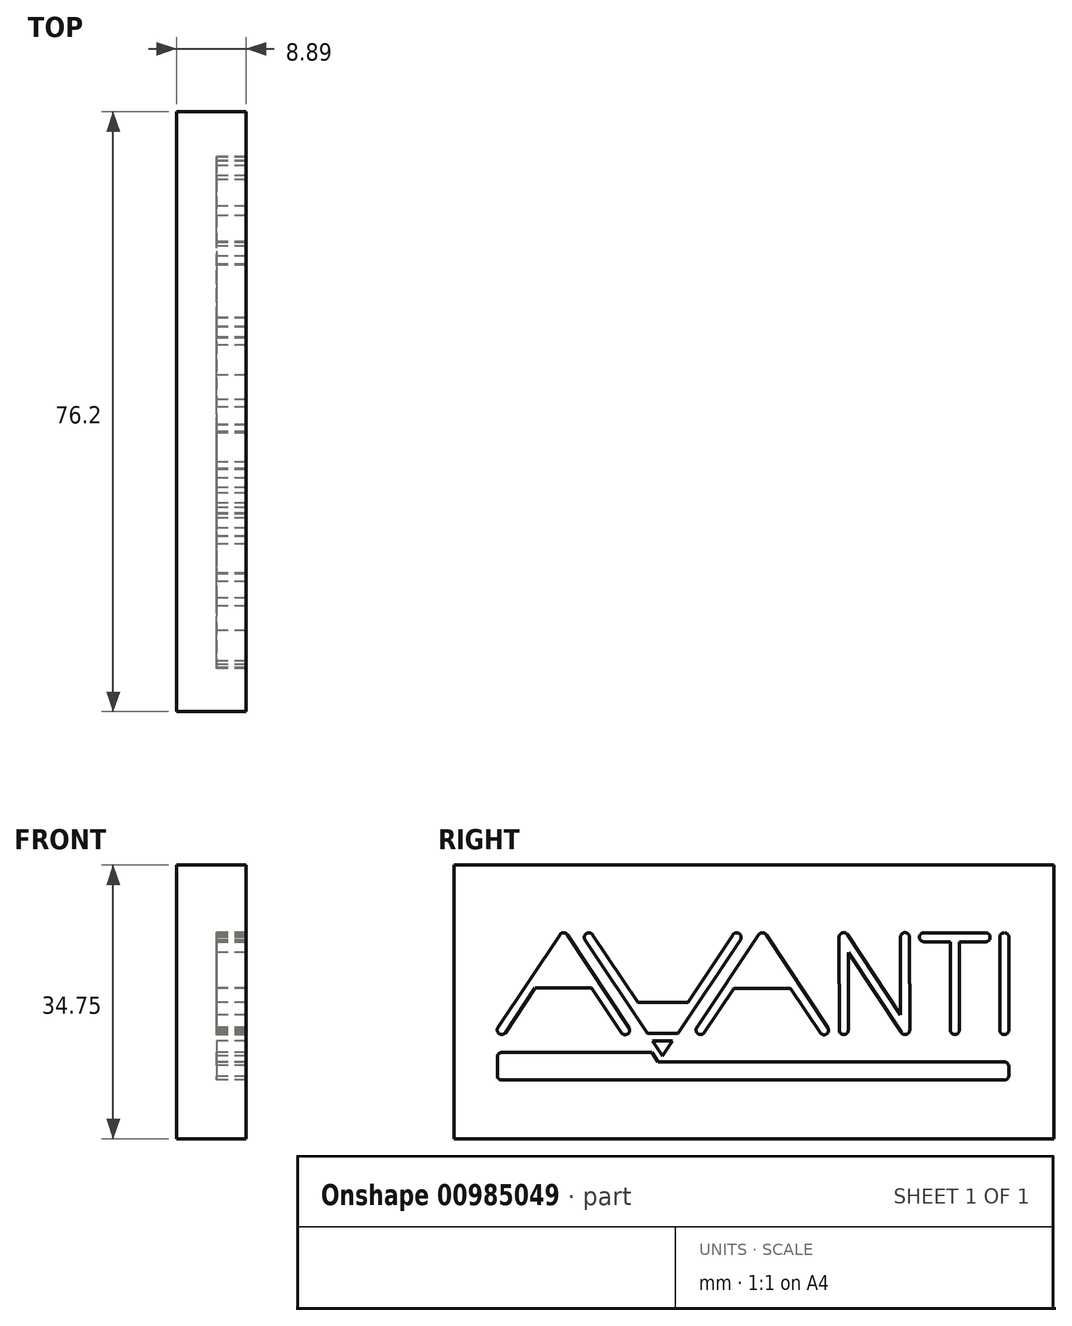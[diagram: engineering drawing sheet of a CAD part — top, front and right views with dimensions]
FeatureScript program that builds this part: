
annotation { "Feature Type Name" : "Feature", "Feature Type Description" : "" }
export const myFeature = defineFeature(function(context is Context, id is Id, definition is map)
    precondition{}
    {
        {
            var Q0;
            Q0=qCreatedBy(makeId("Right.planeOp"),FACE);
            var sketch = newSketch(context, id + "F0", { "sketchPlane" : qUnion([Q0])});
            skArc(sketch, "E0", {"start": v(-1.7, 15.63) * mm, "mid": v(-1.88, 16.42) * mm, "end": v(-2.67, 16.26) * mm});
            skLineSegment(sketch, "E1", {"start": v(-1.7, 15.63) * mm, "end": v(-9.65, 3.71) * mm});
            skLineSegment(sketch, "E2", {"start": v(-9.65, 3.71) * mm, "end": v(-13.5, 3.71) * mm});
            skLineSegment(sketch, "E3", {"start": v(-13.5, 3.71) * mm, "end": v(-21.48, 15.64) * mm});
            skArc(sketch, "E4", {"start": v(-20.5, 16.26) * mm, "mid": v(-21.28, 16.42) * mm, "end": v(-21.48, 15.64) * mm});
            skLineSegment(sketch, "E5", {"start": v(-20.5, 16.26) * mm, "end": v(-14.76, 7.69) * mm});
            skLineSegment(sketch, "E6", {"start": v(-14.76, 7.69) * mm, "end": v(-8.41, 7.69) * mm});
            skLineSegment(sketch, "E7", {"start": v(-8.41, 7.69) * mm, "end": v(-2.67, 16.26) * mm});
            skArc(sketch, "E8", {"start": v(1.57, 16.27) * mm, "mid": v(1.08, 16.52) * mm, "end": v(0.6, 16.27) * mm});
            skLineSegment(sketch, "E9", {"start": v(1.57, 16.27) * mm, "end": v(9.4, 4.42) * mm});
            skArc(sketch, "E10", {"start": v(8.43, 3.81) * mm, "mid": v(9.21, 3.65) * mm, "end": v(9.4, 4.42) * mm});
            skLineSegment(sketch, "E11", {"start": v(4.63, 9.48) * mm, "end": v(8.43, 3.81) * mm});
            skLineSegment(sketch, "E12", {"start": v(-2.54, 9.48) * mm, "end": v(4.63, 9.48) * mm});
            skLineSegment(sketch, "E13", {"start": v(-6.33, 3.8) * mm, "end": v(-2.54, 9.48) * mm});
            skArc(sketch, "E14", {"start": v(-7.25, 4.5) * mm, "mid": v(-7.13, 3.71) * mm, "end": v(-6.33, 3.8) * mm});
            skLineSegment(sketch, "E15", {"start": v(-7.25, 4.5) * mm, "end": v(0.6, 16.27) * mm});
            skLineSegment(sketch, "E16", {"start": v(-12.86, 2.8) * mm, "end": v(-11.6, 0.86) * mm});
            skLineSegment(sketch, "E17", {"start": v(-10.32, 2.8) * mm, "end": v(-12.86, 2.8) * mm});
            skLineSegment(sketch, "E18", {"start": v(-11.6, 0.86) * mm, "end": v(-10.32, 2.8) * mm});
            skLineSegment(sketch, "E19", {"start": v(-32.6, 0.86) * mm, "end": v(-32.6, -1.7) * mm});
            skArc(sketch, "E20", {"start": v(-32.13, 1.3) * mm, "mid": v(-32.42, 1.15) * mm, "end": v(-32.6, 0.86) * mm});
            skLineSegment(sketch, "E21", {"start": v(-12.97, 1.3) * mm, "end": v(-32.13, 1.3) * mm});
            skLineSegment(sketch, "E22", {"start": v(-12.19, 0.1) * mm, "end": v(-12.97, 1.3) * mm});
            skLineSegment(sketch, "E23", {"start": v(31.9, 0.1) * mm, "end": v(-12.19, 0.1) * mm});
            skArc(sketch, "E24", {"start": v(32.36, -0.34) * mm, "mid": v(32.2, -0.05) * mm, "end": v(31.9, 0.1) * mm});
            skLineSegment(sketch, "E25", {"start": v(32.36, -0.34) * mm, "end": v(32.36, -1.73) * mm});
            skArc(sketch, "E26", {"start": v(31.9, -2.18) * mm, "mid": v(32.2, -2.03) * mm, "end": v(32.36, -1.73) * mm});
            skLineSegment(sketch, "E27", {"start": v(-32.1, -2.18) * mm, "end": v(31.9, -2.18) * mm});
            skArc(sketch, "E28", {"start": v(-32.6, -1.7) * mm, "mid": v(-32.43, -2.03) * mm, "end": v(-32.1, -2.18) * mm});
            skLineSegment(sketch, "E29", {"start": v(32.38, 4.15) * mm, "end": v(32.38, 16) * mm});
            skArc(sketch, "E30", {"start": v(31.23, 4.1) * mm, "mid": v(31.83, 3.58) * mm, "end": v(32.38, 4.15) * mm});
            skLineSegment(sketch, "E31", {"start": v(31.23, 15.96) * mm, "end": v(31.23, 4.1) * mm});
            skArc(sketch, "E32", {"start": v(32.38, 16) * mm, "mid": v(31.78, 16.53) * mm, "end": v(31.23, 15.96) * mm});
            skArc(sketch, "E33", {"start": v(-23.7, 16.27) * mm, "mid": v(-24.18, 16.52) * mm, "end": v(-24.67, 16.27) * mm});
            skLineSegment(sketch, "E34", {"start": v(-23.7, 16.27) * mm, "end": v(-15.85, 4.43) * mm});
            skArc(sketch, "E35", {"start": v(-16.83, 3.82) * mm, "mid": v(-16.05, 3.65) * mm, "end": v(-15.85, 4.43) * mm});
            skLineSegment(sketch, "E36", {"start": v(-20.63, 9.48) * mm, "end": v(-16.83, 3.82) * mm});
            skLineSegment(sketch, "E37", {"start": v(-27.8, 9.48) * mm, "end": v(-20.63, 9.48) * mm});
            skLineSegment(sketch, "E38", {"start": v(-31.59, 3.8) * mm, "end": v(-27.8, 9.48) * mm});
            skArc(sketch, "E39", {"start": v(-32.5, 4.51) * mm, "mid": v(-32.39, 3.72) * mm, "end": v(-31.59, 3.8) * mm});
            skLineSegment(sketch, "E40", {"start": v(-32.5, 4.51) * mm, "end": v(-24.67, 16.27) * mm});
            skArc(sketch, "E41", {"start": v(24.94, 4.17) * mm, "mid": v(25.48, 3.6) * mm, "end": v(26.09, 4.11) * mm});
            skLineSegment(sketch, "E42", {"start": v(24.94, 4.17) * mm, "end": v(24.94, 15.37) * mm});
            skLineSegment(sketch, "E43", {"start": v(24.94, 15.37) * mm, "end": v(21.57, 15.38) * mm});
            skArc(sketch, "E44", {"start": v(21.58, 16.52) * mm, "mid": v(21.02, 15.96) * mm, "end": v(21.57, 15.38) * mm});
            skLineSegment(sketch, "E45", {"start": v(21.58, 16.52) * mm, "end": v(29.43, 16.52) * mm});
            skArc(sketch, "E46", {"start": v(29.48, 15.37) * mm, "mid": v(30, 15.97) * mm, "end": v(29.43, 16.52) * mm});
            skLineSegment(sketch, "E47", {"start": v(29.48, 15.37) * mm, "end": v(26.11, 15.37) * mm});
            skLineSegment(sketch, "E48", {"start": v(26.11, 15.37) * mm, "end": v(26.09, 4.11) * mm});
            skArc(sketch, "E49", {"start": v(19.77, 16) * mm, "mid": v(19.18, 16.53) * mm, "end": v(18.62, 15.96) * mm});
            skLineSegment(sketch, "E50", {"start": v(19.77, 16) * mm, "end": v(19.79, 4.13) * mm});
            skArc(sketch, "E51", {"start": v(18.72, 3.83) * mm, "mid": v(19.36, 3.6) * mm, "end": v(19.79, 4.13) * mm});
            skLineSegment(sketch, "E52", {"start": v(18.72, 3.83) * mm, "end": v(11.99, 14) * mm});
            skLineSegment(sketch, "E53", {"start": v(11.99, 14) * mm, "end": v(11.98, 4.16) * mm});
            skArc(sketch, "E54", {"start": v(10.83, 4.11) * mm, "mid": v(11.43, 3.58) * mm, "end": v(11.98, 4.16) * mm});
            skLineSegment(sketch, "E55", {"start": v(10.83, 4.11) * mm, "end": v(10.82, 15.96) * mm});
            skArc(sketch, "E56", {"start": v(11.87, 16.3) * mm, "mid": v(11.22, 16.5) * mm, "end": v(10.82, 15.96) * mm});
            skLineSegment(sketch, "E57", {"start": v(11.87, 16.3) * mm, "end": v(18.61, 6.1) * mm});
            skLineSegment(sketch, "E58", {"start": v(18.61, 6.1) * mm, "end": v(18.62, 15.96) * mm});
            skLineSegment(sketch, "E59", {"start": v(-38.1, 40.64) * mm, "end": v(-38.1, -40.64) * mm});
            skLineSegment(sketch, "E60", {"start": v(38.1, 40.64) * mm, "end": v(38.1, -40.64) * mm});
            skLineSegment(sketch, "E61", {"start": v(-38.1, -9.64) * mm, "end": v(38.1, -9.64) * mm});
            skLineSegment(sketch, "E62", {"start": v(38.1, -9.64) * mm, "end": v(38.1, 25.1) * mm});
            skLineSegment(sketch, "E63", {"start": v(38.1, 25.1) * mm, "end": v(-38.1, 25.1) * mm});
            skSolve(sketch);
        }
        {
            var Q0;
            Q0=makeQuery(id+"F0.imprint","IMPRINT",FACE,{"disambiguationData":[TD([[makeQuery(id+"F0.imprint","IMPRINT",EDGE,{"derivedFrom":sQuery(id+"F0.wireOp",EDGE,"E0")}),-1.0]])]});
            extrude(context, id + "F1", {"entities" : qUnion([Q0]), "depth" : 8.9 * mm, "offsetDistance" : 25.4 * mm});
        }
        {
            var Q0;
            Q0=makeQuery(id+"F0.imprint","IMPRINT",FACE,{"disambiguationData":[TD([[makeQuery(id+"F0.imprint","IMPRINT",EDGE,{"derivedFrom":sQuery(id+"F0.wireOp",EDGE,"E8")}),1.0]])]});
            var Q1;
            Q1=makeQuery(id+"F0.imprint","IMPRINT",FACE,{"disambiguationData":[TD([[makeQuery(id+"F0.imprint","IMPRINT",EDGE,{"derivedFrom":sQuery(id+"F0.wireOp",EDGE,"E19")}),1.0]])]});
            var Q2;
            Q2=makeQuery(id+"F0.imprint","IMPRINT",FACE,{"disambiguationData":[TD([[makeQuery(id+"F0.imprint","IMPRINT",EDGE,{"derivedFrom":sQuery(id+"F0.wireOp",EDGE,"E0")}),1.0]])]});
            var Q3;
            Q3=makeQuery(id+"F0.imprint","IMPRINT",FACE,{"disambiguationData":[TD([[makeQuery(id+"F0.imprint","IMPRINT",EDGE,{"derivedFrom":sQuery(id+"F0.wireOp",EDGE,"E16")}),1.0]])]});
            var Q4;
            Q4=makeQuery(id+"F0.imprint","IMPRINT",FACE,{"disambiguationData":[TD([[makeQuery(id+"F0.imprint","IMPRINT",EDGE,{"derivedFrom":sQuery(id+"F0.wireOp",EDGE,"E49")}),1.0]])]});
            var Q5;
            Q5=makeQuery(id+"F0.imprint","IMPRINT",FACE,{"disambiguationData":[TD([[makeQuery(id+"F0.imprint","IMPRINT",EDGE,{"derivedFrom":sQuery(id+"F0.wireOp",EDGE,"E41")}),1.0]])]});
            var Q6;
            Q6=makeQuery(id+"F0.imprint","IMPRINT",FACE,{"disambiguationData":[TD([[makeQuery(id+"F0.imprint","IMPRINT",EDGE,{"derivedFrom":sQuery(id+"F0.wireOp",EDGE,"E29")}),1.0]])]});
            var Q7;
            Q7=makeQuery(id+"F0.imprint","IMPRINT",FACE,{"disambiguationData":[TD([[makeQuery(id+"F0.imprint","IMPRINT",EDGE,{"derivedFrom":sQuery(id+"F0.wireOp",EDGE,"E33")}),1.0]])]});
            extrude(context, id + "F2", {"entities" : qUnion([Q0, Q1, Q2, Q3, Q4, Q5, Q6, Q7]), "operationType" : NewBodyOperationType.ADD, "depth" : 5.08 * mm, "offsetDistance" : 25.4 * mm});
        }
    });
